# Revit family: ge-p1080_2100mg7_50Hz
name_source: partatom
category: 機械設備
units: mm (PartAtom-declared; Revit-internal decimal feet)

## family parameters
OmniClass タイトル = Split System Air Conditioning Units
OmniClass 番号 = 23.75.10.24.21.27.27
パーツ タイプ = 標準
ロード時にボイドで切り取り = いいえ
丸型コネクタ寸法 = 直径を使用
作業面ベース = いいえ
共有 = いいえ
常に垂直 = はい
部屋計算ポイント = はい

## types (3) — shared parameters
Depth = 1400  [stored 4.59318 ft]
Height = 470  [stored 1.54199 ft]
IfcExportAs = IfcUnitaryEquipmentType
IfcExportType = AIRCONDITIONINGUNIT
OmniClassCode = 23-33 17 13 11
URL = https://www.mitsubishielectric.co.jp
Uniclass2015Code = Pr_70_65_03_84
Uniclass2015Title = Split coil remote air cooled condensing units
Uniclass2015Version = Systems v1.9
h = 25  [stored 0.082021 ft]
j = 25  [stored 0.082021 ft]
ダクト1高 = 300
ダクト2高 = 400  [stored 1.31234 ft]
ドレン管径 = 32.00 mm
仕様書バージョン = Version1.0
企業コード = 108420
冷媒液管径 = 9.52 mm
冷媒管径 = 100.00 mm
冷媒高低圧ガス管径 = 0.00 mm
分類コード = 50053003221160
加湿給水管径 = 21.70 mm
参照している仕様書等のバージョン = 公共建築工事標準仕様書（機械設備工事編）平成31年度版
周波数 = 50 Hz
呼称 = 室内機_外気処理エアコン(天井吊形)
外気量 = 0.0 m³/h
始動方式 = 直入
形式 = 外気処理エアコン(天井吊形)
排気量 = 0.0 m³/h
本体マテリアル = <カテゴリ別>
極数 = 1
法定耐用年数 = 15
消費電力_加湿器 = 0 W
消費電力_電気ヒーター = 0 W
相 = 1
相_電気ヒーター = 1
積算_科目 = 1 空気調和設備
符号 = ACP-CIO
給気量 = 0.0 m³/h
製品リリース年月 = 2020年7月22日
製品出荷対象 = 国内
製造元 = 三菱電機株式会社
設置方法 = 天井吊形
説明 = ビル用マルチエアコン 室内ユニット 天井埋込外気処理
負荷分類 = 10_ファンコイル類
運転質量 = 0.00 kg
電圧 = 200 V
電圧_電気ヒーター = 0 V

## per-type parameters (varying)
| type | L | Width | ダクト1幅 | ダクト2幅 | 冷媒ガス管径 | 冷媒管径符号 | 冷房能力 | 暖房能力 | 有効加湿量 | 機外静圧 | 消費電力 | 消費電力_冷房 | 消費電力_暖房 | 製品質量 | 質量 | 電動機出力_送風機 | 音響パワーレベル(dB) | 風量 |
| GE-P1080MG7 | 950  [stored 3.1168 ft] | 850  [stored 2.78871 ft] | 600 | 700  [stored 2.29659 ft] | 15.88 mm | Bd | 14 kW | 14 kW | 8.3 | 210.0 Pa | 240 W | 240 W | 240 W | 97.00 kg | 116.40 kg | 200 W | 63 | 1080.0 m³/h |
| GE-P1680MG7 | 1350  [stored 4.42913 ft] | 1250  [stored 4.10105 ft] | 1000  [stored 3.28084 ft] | 1100 | 19.05 mm | Be | 22 kW | 21 kW | 13 | 210.0 Pa | 420 W | 420 W | 420 W | 114.00 kg | 136.80 kg | 400 W | 67 | 1680.0 m³/h |
| GE-P2100MG7 | 1350  [stored 4.42913 ft] | 1250  [stored 4.10105 ft] | 1000  [stored 3.28084 ft] | 1100 | 22.20 mm | Bf | 28 kW | 27 kW | 16.2 | 170.0 Pa | 490 W | 490 W | 490 W | 121.00 kg | 145.20 kg | 400 W | 71 | 2100.0 m³/h |

note: column(s) folded — value = type name in every type: モデル

note: [stored X ft] marks values corroborated as IEEE doubles in the binary element streams (Revit-internal decimal feet)
